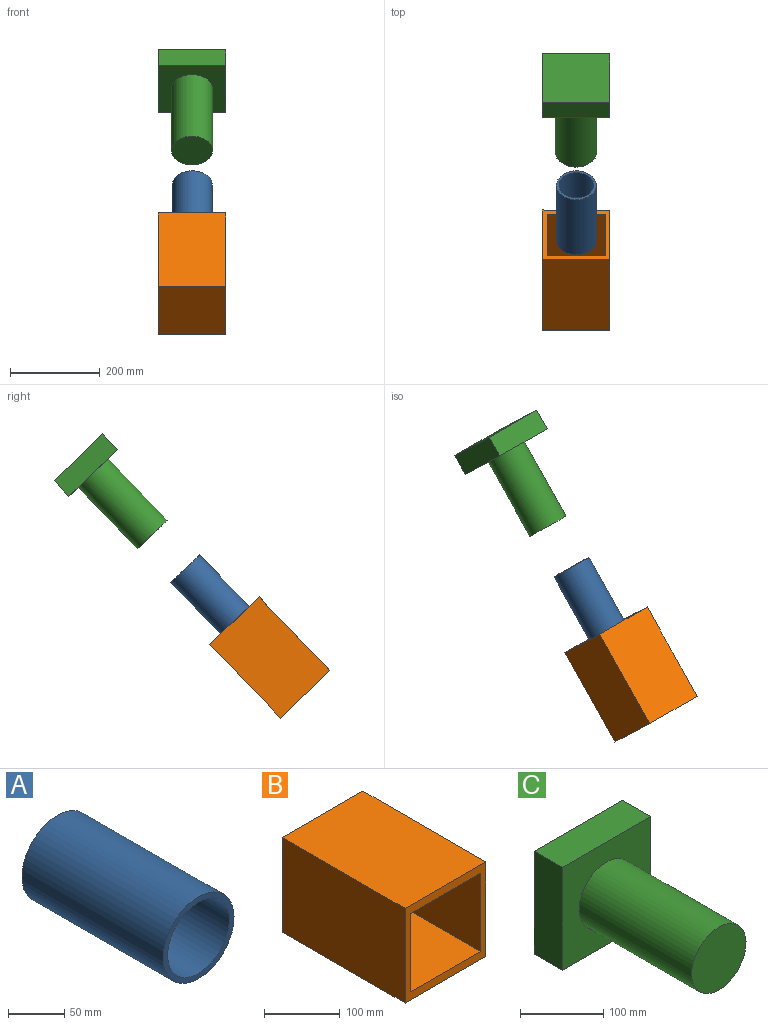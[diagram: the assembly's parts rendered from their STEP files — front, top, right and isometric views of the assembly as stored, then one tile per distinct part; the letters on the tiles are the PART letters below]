
ASSEMBLY  parts=3 mates=2
PART A: 4 faces, bbox 89.4x177.8x89.4 mm
  f0: cylinder r=44.69mm len=177.8mm, axis (0,1,0), area 49925.8mm2, adj f1,f2
  f1: plane 89.38x89.38mm, normal (0,1,0), area 1524.1mm2, adj f0,f3
  f2: plane 89.38x89.38mm, normal (0,-1,0), area 1524.1mm2, adj f0,f3
  f3: cylinder r=38.89mm len=177.8mm, axis (0,-1,0), area 43440.8mm2, adj f1,f2
PART B: 11 faces, bbox 150.2x228.6x152.5 mm
  f0: plane 152.51x150.17mm, normal (0,-1,0), area 6403.7mm2, adj f1,f2,f3,f4,f6,f7,f8,f9
  f1: plane 228.6x150.17mm, normal (0,0,1), area 34329.8mm2, adj f0,f2,f4,f5
  f2: plane 228.6x152.51mm, normal (-1,0,0), area 34863.3mm2, adj f0,f1,f3,f5
  f3: plane 228.6x150.17mm, normal (0,0,-1), area 34329.8mm2, adj f0,f2,f4,f5
  f4: plane 228.6x152.51mm, normal (1,0,0), area 34863.3mm2, adj f0,f1,f3,f5
  f5: plane 152.51x150.17mm, normal (0,1,0), area 22902.7mm2, adj f1,f2,f3,f4
  f6: plane 205.28x130.58mm, normal (0,0,-1), area 26804.8mm2, adj f0,f7,f9,f10
  f7: plane 205.28x126.36mm, normal (1,0,0), area 25938.6mm2, adj f0,f6,f8,f10
  f8: plane 205.28x130.58mm, normal (0,0,1), area 26804.8mm2, adj f0,f7,f9,f10
  f9: plane 205.28x126.36mm, normal (-1,0,0), area 25938.6mm2, adj f0,f6,f8,f10
  f10: plane 130.58x126.36mm, normal (0,-1,0), area 16499mm2, adj f6,f7,f8,f9
PART C: 8 faces, bbox 149.9x238.8x151.1 mm
  f0: cylinder r=46.16mm len=190.96mm, axis (0,1,0), area 55377.7mm2, adj f1,f7
  f1: plane 92.31x92.31mm, normal (0,-1,0), area 6692.6mm2, adj f0
  f2: plane 151.12x47.88mm, normal (1,0,0), area 7235mm2, adj f3,f5,f6,f7
  f3: plane 149.88x47.88mm, normal (0,0,1), area 7175.7mm2, adj f2,f4,f6,f7
  f4: plane 151.12x47.88mm, normal (-1,0,0), area 7235mm2, adj f3,f5,f6,f7
  f5: plane 149.88x47.88mm, normal (0,0,-1), area 7175.7mm2, adj f2,f4,f6,f7
  f6: plane 151.12x149.88mm, normal (0,1,0), area 22648.7mm2, adj f2,f3,f4,f5
  f7: plane 151.12x149.88mm, normal (0,-1,0), area 15956.2mm2, adj f0,f2,f3,f4,f5
PLACE A rot(axis=(-1,0,0),133.7deg) t=(-202.67,-237.44,343.14)mm
PLACE B rot(axis=(-1,0,0),133.7deg) t=(-202.84,-382.43,190.29)mm
PLACE C rot(axis=(1,0,0),46.3deg) t=(-203.57,91.22,685.66)mm
MATE cylindrical C.f0 <-> B.f5  axis (0,-0.69,-0.72) through (-203.57,-40.79,547.69)mm
MATE cylindrical B.f10 <-> A.f0  axis (0,0.69,0.72) through (-202.67,-366.97,207.77)mm
